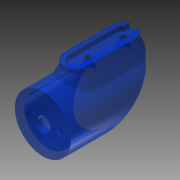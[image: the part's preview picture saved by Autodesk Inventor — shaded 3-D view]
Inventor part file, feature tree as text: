
AUTODESK INVENTOR PART (.ipt)
format: ipt  version: 2014 (Build 180170000, 170)  size: 231,424 bytes
history: native  units: in
note: dims shown in document units (in); Inventor stores cm internally (conversion verified against a paired STEP export)
features: sketch x11, extrude x10, plane x4, chamfer x2, hole x1, other x1
ambient origin geometry x8: Origin, YZ Plane, XZ Plane, XY Plane, X Axis, Y Axis, Z Axis, Center Point
bodies: Solid1 (feature_tree)
feature tree (29):
  extrude  "Extrusion1"  Depth=0.27in
  hole  "Hole1"  [1 undecoded]
  extrude  "Extrusion2"  Depth=0.185in
  chamfer  "Chamfer1"  Distance=0.02in
  chamfer  "Chamfer2"  Distance=0.015in Angle=45.0deg
  extrude  "Extrusion3"  Depth=0.1in
  plane  "Work Plane1"
  plane  "Work Plane2"
  extrude  "Extrusion4"  TaperAngle=45.0deg  [1 undecoded]
  plane  "Work Plane4"
  extrude  "Extrusion5"  [1 undecoded]
  extrude  "Extrusion6"  Depth=0.5in
  extrude  "Extrusion7"  Depth=1.0in
  extrude  "Extrusion8"  Depth=0.1in
  extrude  "Extrusion9"  Depth=0.1in TaperAngle=0.0deg
  extrude  "Extrusion10"  Depth=0.2in
  sketch  "Sketch1"  dims[d0=0.985in d1=0.27in]
  sketch  "Sketch2"  dims[d2=0.1in d3=0.0in d4=0.675in]
  sketch  "Sketch3"  dims[d5=0.3375in]
  sketch  "Sketch4"  dims[d6=0.097in d7=0.75in d8=0.375in d9=0.25in d10=0.5635in d11=1.0in d12=0.8108in d13=0.185in]
  other  "Work Axis1"
  sketch  "Sketch6"  dims[d14=0.659in]
  plane  "Work Plane3"
  sketch  "Sketch7"  dims[d15=0.3295in d16=0.02in d17=0.0in d18=0.015in d19=0.125in d20=45.0deg]
  sketch  "Sketch8"  dims[d21=0.03in d22=0.125in d23=45.0deg d24=0.1in]
  sketch  "Sketch9"  dims[d25=0.747in d26=0.0in d27=45.0deg]
  sketch  "Sketch10"  dims[d28=0.0in d29=0.0in d30=-0.15in]
  sketch  "Sketch11"  dims[d31=1.0in d32=0.5in]
  sketch  "Sketch12"  dims[d33=0.6in d34=1.0in d35=0.1718in d36=0.1in d37=0.1in d38=0.0in d39=0.2in d40=0.1in d41=0.0in d42=0.75in d43=0.12in d44=0.25in d45=0.5in d46=0.0in d47=0.232in d48=0.5in d49=0.0in d50=1.0in d51=0.0in]
note: 3 required parameter values undecoded (feature->parameter linkage not recoverable at this tier; creation-order binding heuristic only, values carry confidence <= 0.55)
